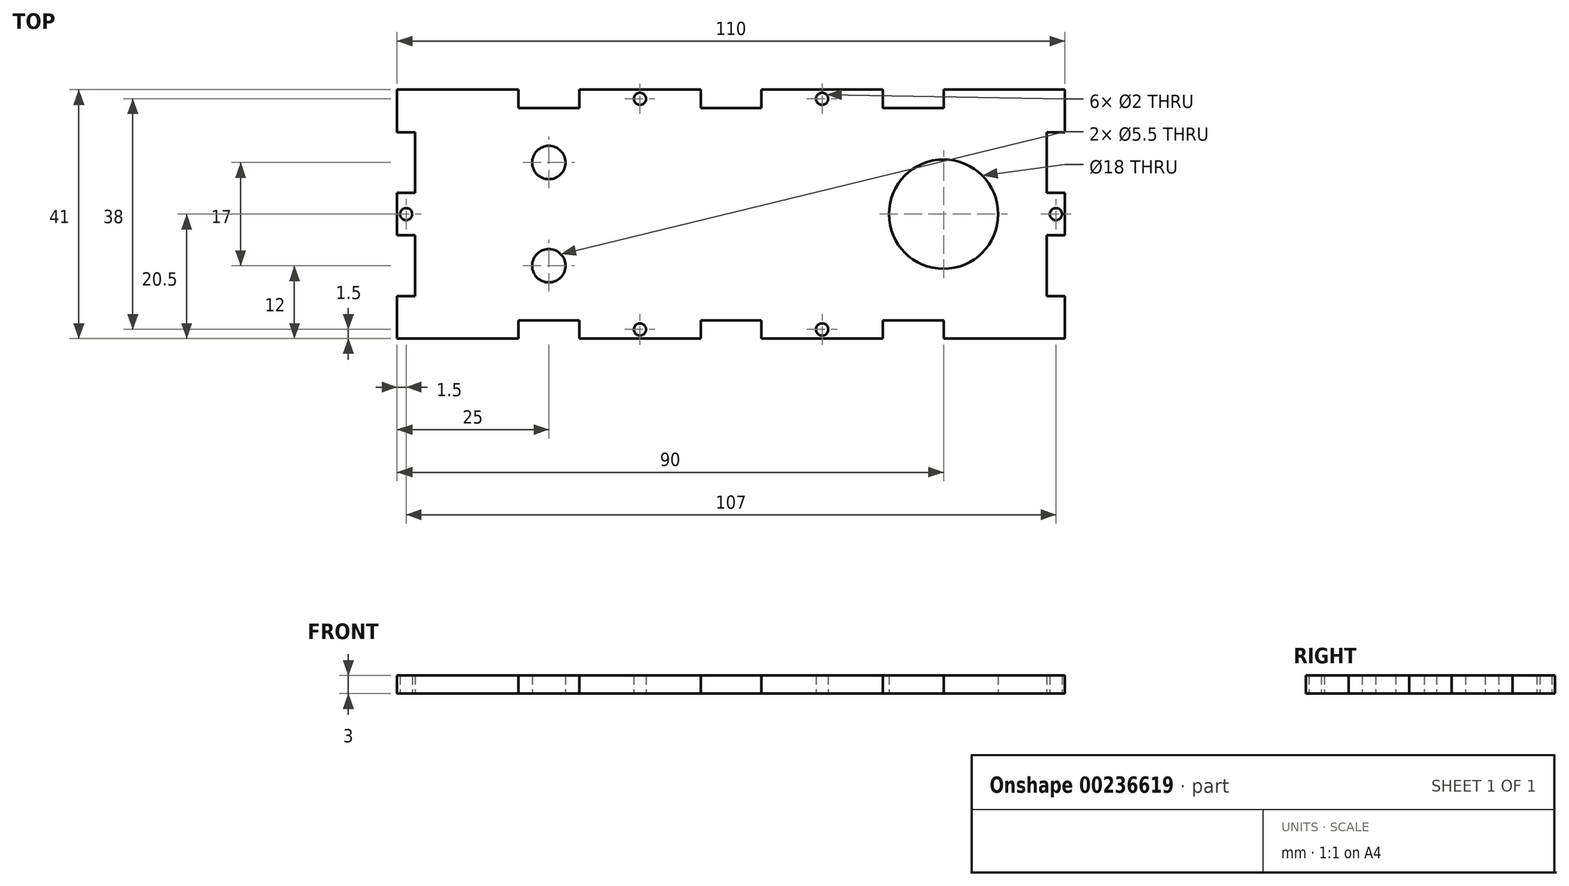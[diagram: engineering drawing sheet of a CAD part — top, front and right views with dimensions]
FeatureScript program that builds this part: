
annotation { "Feature Type Name" : "Feature", "Feature Type Description" : "" }
export const myFeature = defineFeature(function(context is Context, id is Id, definition is map)
    precondition{}
    {
        {
            var Q0;
            Q0=qCreatedBy(makeId("Top.planeOp"),FACE);
            var sketch = newSketch(context, id + "F0", { "sketchPlane" : qUnion([Q0])});
            skLineSegment(sketch, "E0", {"start": v(0, 0) * mm, "end": v(0, 7) * mm});
            skLineSegment(sketch, "E1", {"start": v(0, 7) * mm, "end": v(3, 7) * mm});
            skLineSegment(sketch, "E2", {"start": v(3, 7) * mm, "end": v(3, 17) * mm});
            skLineSegment(sketch, "E3", {"start": v(3, 17) * mm, "end": v(0, 17) * mm});
            skLineSegment(sketch, "E4", {"start": v(0, 17) * mm, "end": v(0, 24) * mm});
            skLineSegment(sketch, "E5", {"start": v(0, 24) * mm, "end": v(3, 24) * mm});
            skLineSegment(sketch, "E6", {"start": v(3, 24) * mm, "end": v(3, 34) * mm});
            skLineSegment(sketch, "E7", {"start": v(3, 34) * mm, "end": v(0, 34) * mm});
            skLineSegment(sketch, "E8", {"start": v(0, 34) * mm, "end": v(0, 41) * mm});
            skLineSegment(sketch, "E9", {"start": v(0, 41) * mm, "end": v(20, 41) * mm});
            skLineSegment(sketch, "E10", {"start": v(20, 41) * mm, "end": v(20, 38) * mm});
            skLineSegment(sketch, "E11", {"start": v(20, 38) * mm, "end": v(30, 38) * mm});
            skLineSegment(sketch, "E12", {"start": v(30, 38) * mm, "end": v(30, 41) * mm});
            skLineSegment(sketch, "E13", {"start": v(30, 41) * mm, "end": v(50, 41) * mm});
            skLineSegment(sketch, "E14", {"start": v(50, 38) * mm, "end": v(55, 38) * mm});
            skLineSegment(sketch, "E15", {"start": v(50, 41) * mm, "end": v(50, 38) * mm});
            skLineSegment(sketch, "E16", {"start": v(55, 40.92) * mm, "end": v(55, 0) * mm, "construction": true});
            skLineSegment(sketch, "E17", {"start": v(0, 20.5) * mm, "end": v(55, 20.5) * mm, "construction": true});
            skCircle(sketch, "E18", {"center": v(40, 39.5) * mm, "radius": 1 * mm});
            skPoint(sketch, "E18.centerSnap0", {"position": v(40, 41) * mm});
            skPoint(sketch, "E18.centerSnap1", {"position": v(50, 39.5) * mm});
            skCircle(sketch, "E19", {"center": v(1.5, 20.5) * mm, "radius": 1 * mm});
            skPoint(sketch, "E19.centerSnap0", {"position": v(1.5, 24) * mm});
            skLineSegment(sketch, "E20.MirrorCS", {"start": v(20, 0) * mm, "end": v(20, 3) * mm});
            skLineSegment(sketch, "E21.MirrorCS", {"start": v(50, 0) * mm, "end": v(50, 3) * mm});
            skLineSegment(sketch, "E22.MirrorCS", {"start": v(30, 3) * mm, "end": v(30, 0) * mm});
            skCircle(sketch, "E23.MirrorC", {"center": v(40, 1.5) * mm, "radius": 1 * mm});
            skLineSegment(sketch, "E24.MirrorCS", {"start": v(20, 3) * mm, "end": v(30, 3) * mm});
            skLineSegment(sketch, "E25.MirrorCS", {"start": v(30, 0) * mm, "end": v(50, 0) * mm});
            skPoint(sketch, "E26.MirrorP", {"position": v(40, 0) * mm});
            skPoint(sketch, "E27.MirrorP", {"position": v(50, 1.5) * mm});
            skLineSegment(sketch, "E28.MirrorCS", {"start": v(0, 0) * mm, "end": v(20, 0) * mm});
            skLineSegment(sketch, "E29.MirrorCS", {"start": v(50, 3) * mm, "end": v(55, 3) * mm});
            skLineSegment(sketch, "E30.MirrorCS", {"start": v(60, 41) * mm, "end": v(60, 38) * mm});
            skLineSegment(sketch, "E31.MirrorCS", {"start": v(107, 34) * mm, "end": v(110, 34) * mm});
            skLineSegment(sketch, "E32.MirrorCS", {"start": v(110, 24) * mm, "end": v(107, 24) * mm});
            skLineSegment(sketch, "E33.MirrorCS", {"start": v(110, 7) * mm, "end": v(107, 7) * mm});
            skLineSegment(sketch, "E34.MirrorCS", {"start": v(107, 17) * mm, "end": v(110, 17) * mm});
            skLineSegment(sketch, "E35.MirrorCS", {"start": v(90, 41) * mm, "end": v(90, 38) * mm});
            skLineSegment(sketch, "E36.MirrorCS", {"start": v(80, 38) * mm, "end": v(80, 41) * mm});
            skLineSegment(sketch, "E37.MirrorCS", {"start": v(60, 0) * mm, "end": v(60, 3) * mm});
            skCircle(sketch, "E38.MirrorC", {"center": v(108.5, 20.5) * mm, "radius": 1 * mm});
            skCircle(sketch, "E39.MirrorC", {"center": v(70, 1.5) * mm, "radius": 1 * mm});
            skCircle(sketch, "E40.MirrorC", {"center": v(70, 39.5) * mm, "radius": 1 * mm});
            skLineSegment(sketch, "E41.MirrorCS", {"start": v(110, 17) * mm, "end": v(110, 24) * mm});
            skLineSegment(sketch, "E42.MirrorCS", {"start": v(80, 41) * mm, "end": v(60, 41) * mm});
            skPoint(sketch, "E43.MirrorP", {"position": v(108.5, 24) * mm});
            skLineSegment(sketch, "E44.MirrorCS", {"start": v(90, 3) * mm, "end": v(80, 3) * mm});
            skLineSegment(sketch, "E45.MirrorCS", {"start": v(110, 0) * mm, "end": v(90, 0) * mm});
            skPoint(sketch, "E46.MirrorP", {"position": v(70, 41) * mm});
            skLineSegment(sketch, "E47.MirrorCS", {"start": v(107, 24) * mm, "end": v(107, 34) * mm});
            skPoint(sketch, "E48.MirrorP", {"position": v(60, 39.5) * mm});
            skLineSegment(sketch, "E49.MirrorCS", {"start": v(110, 0) * mm, "end": v(110, 7) * mm});
            skPoint(sketch, "E50.MirrorP", {"position": v(70, 0) * mm});
            skLineSegment(sketch, "E51.MirrorCS", {"start": v(110, 34) * mm, "end": v(110, 41) * mm});
            skLineSegment(sketch, "E52.MirrorCS", {"start": v(107, 7) * mm, "end": v(107, 17) * mm});
            skLineSegment(sketch, "E53.MirrorCS", {"start": v(110, 41) * mm, "end": v(90, 41) * mm});
            skLineSegment(sketch, "E54.MirrorCS", {"start": v(90, 38) * mm, "end": v(80, 38) * mm});
            skLineSegment(sketch, "E55.MirrorCS", {"start": v(80, 0) * mm, "end": v(60, 0) * mm});
            skLineSegment(sketch, "E56.MirrorCS", {"start": v(80, 3) * mm, "end": v(80, 0) * mm});
            skLineSegment(sketch, "E57.MirrorCS", {"start": v(90, 0) * mm, "end": v(90, 3) * mm});
            skPoint(sketch, "E58.MirrorP", {"position": v(60, 1.5) * mm});
            skLineSegment(sketch, "E59.MirrorCS", {"start": v(60, 3) * mm, "end": v(55, 3) * mm});
            skLineSegment(sketch, "E60.MirrorCS", {"start": v(60, 38) * mm, "end": v(55, 38) * mm});
            skCircle(sketch, "E61", {"center": v(90, 20.5) * mm, "radius": 9 * mm});
            skPoint(sketch, "E61.centerSnap0", {"position": v(110, 20.5) * mm});
            skCircle(sketch, "E62", {"center": v(25, 29) * mm, "radius": 2.75 * mm});
            skPoint(sketch, "E62.centerSnap0", {"position": v(3, 29) * mm});
            skPoint(sketch, "E62.centerSnap1", {"position": v(25, 38) * mm});
            skCircle(sketch, "E63", {"center": v(25, 12) * mm, "radius": 2.75 * mm});
            skPoint(sketch, "E63.centerSnap0", {"position": v(3, 12) * mm});
            skPoint(sketch, "E63.centerSnap1", {"position": v(25, 3) * mm});
            skSolve(sketch);
        }
        {
            var Q0;
            Q0=qSketchRegion(id+"F0",true);
            extrude(context, id + "F1", {"entities" : qUnion([Q0]), "depth" : 3 * mm});
        }
    });
